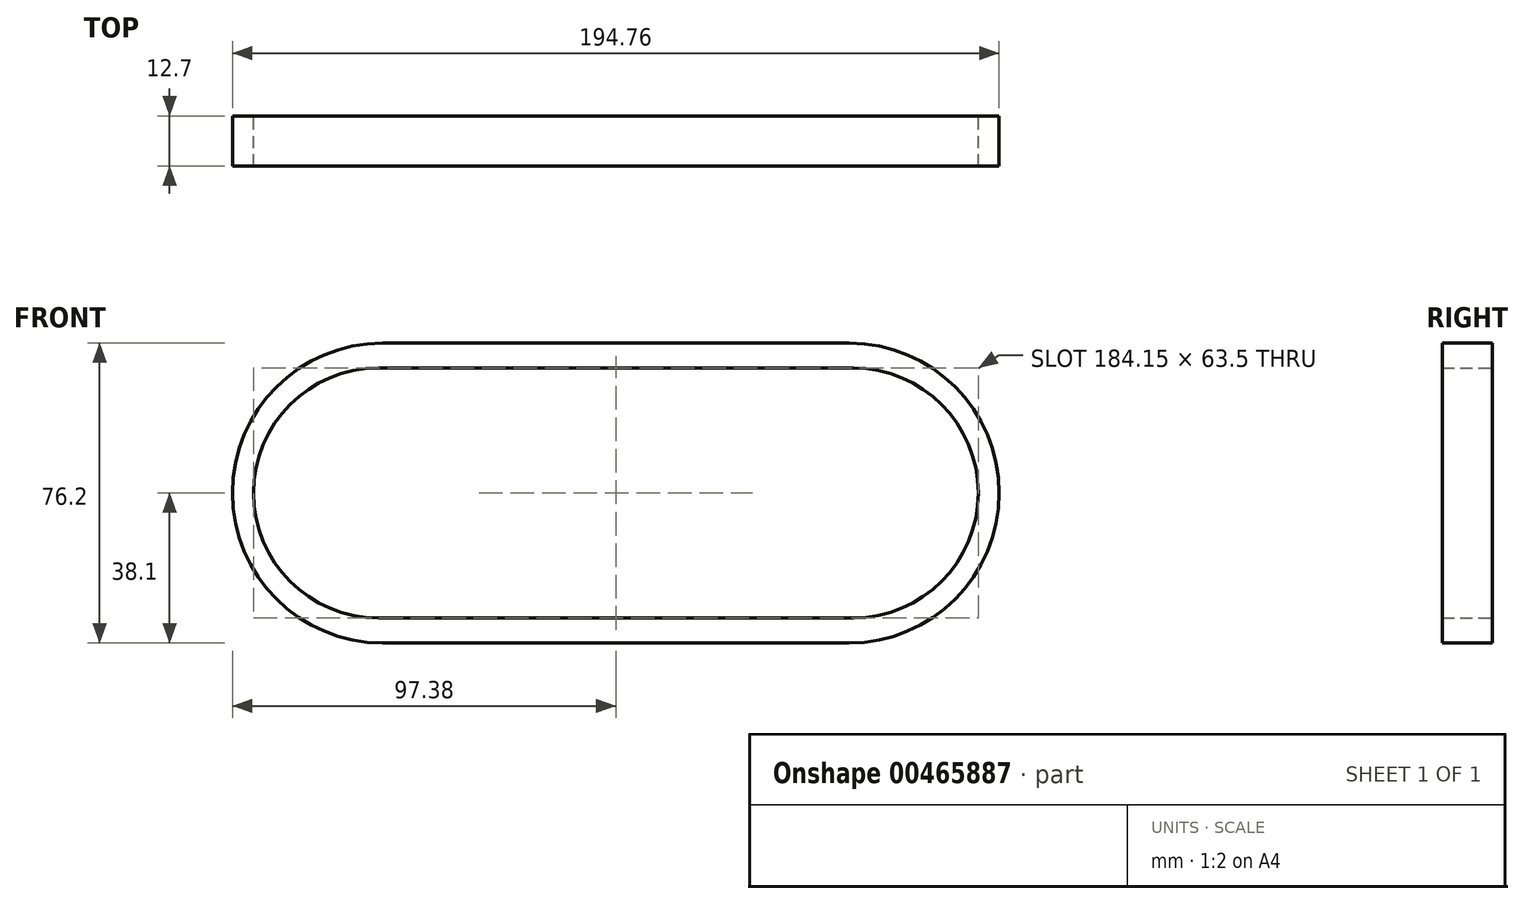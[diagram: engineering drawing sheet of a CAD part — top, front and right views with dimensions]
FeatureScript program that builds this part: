
annotation { "Feature Type Name" : "Feature", "Feature Type Description" : "" }
export const myFeature = defineFeature(function(context is Context, id is Id, definition is map)
    precondition{}
    {
        {
            var Q0;
            Q0=qCreatedBy(makeId("Front.planeOp"),FACE);
            var sketch = newSketch(context, id + "F0", { "sketchPlane" : qUnion([Q0])});
            skLineSegment(sketch, "E0.bottom", {"start": v(-59.28, 38.1) * mm, "end": v(59.28, 38.1) * mm});
            skLineSegment(sketch, "E0.top", {"start": v(-59.28, -38.1) * mm, "end": v(59.28, -38.1) * mm});
            skLineSegment(sketch, "E0.left", {"start": v(-59.28, 38.1) * mm, "end": v(-59.28, -38.1) * mm});
            skLineSegment(sketch, "E0.right", {"start": v(59.28, 38.1) * mm, "end": v(59.28, -38.1) * mm});
            skPoint(sketch, "E0.middle", {"position": v(0, 0) * mm});
            skLineSegment(sketch, "E1", {"start": v(-59.28, 38.1) * mm, "end": v(-59.28, 0) * mm});
            skCircle(sketch, "E2", {"center": v(-59.28, 0) * mm, "radius": 38.1 * mm});
            skLineSegment(sketch, "E3", {"start": v(59.28, 38.1) * mm, "end": v(59.28, 0) * mm});
            skCircle(sketch, "E4", {"center": v(59.28, 0) * mm, "radius": 38.1 * mm});
            skSolve(sketch);
        }
        {
            var Q0;
            {var subQ0=sQuery(id+"F0.wireOp",EDGE,"E0.left");Q0=makeQuery(id+"F0.imprint","IMPRINT",FACE,{"disambiguationData":[TD([[makeQuery(id+"F0.imprint","IMPRINT",EDGE,{"derivedFrom":subQ0}),-1.0]])]});}
            var Q1;
            {var subQ0=sQuery(id+"F0.wireOp",EDGE,"E0.left");Q1=makeQuery(id+"F0.imprint","IMPRINT",FACE,{"disambiguationData":[TD([[makeQuery(id+"F0.imprint","IMPRINT",EDGE,{"derivedFrom":subQ0}),1.0]])]});}
            var Q2;
            {var subQ0=sQuery(id+"F0.wireOp",EDGE,"E0.bottom");Q2=makeQuery(id+"F0.imprint","IMPRINT",FACE,{"disambiguationData":[TD([[makeQuery(id+"F0.imprint","IMPRINT",EDGE,{"derivedFrom":subQ0}),-1.0]])]});}
            var Q3;
            {var subQ0=sQuery(id+"F0.wireOp",EDGE,"E0.right");Q3=makeQuery(id+"F0.imprint","IMPRINT",FACE,{"disambiguationData":[TD([[makeQuery(id+"F0.imprint","IMPRINT",EDGE,{"derivedFrom":subQ0}),-1.0]])]});}
            var Q4;
            {var subQ0=sQuery(id+"F0.wireOp",EDGE,"E0.right");Q4=makeQuery(id+"F0.imprint","IMPRINT",FACE,{"disambiguationData":[TD([[makeQuery(id+"F0.imprint","IMPRINT",EDGE,{"derivedFrom":subQ0}),1.0]])]});}
            extrude(context, id + "F1", {"entities" : qUnion([Q0, Q1, Q2, Q3, Q4]), "depth" : 12.7 * mm, "offsetDistance" : 25.4 * mm});
        }
        {
            var Q0;
            Q0=qCreatedBy(makeId("Front.planeOp"),FACE);
            var sketch = newSketch(context, id + "F2", { "sketchPlane" : qUnion([Q0])});
            skLineSegment(sketch, "E5.bottom", {"start": v(60.33, 31.75) * mm, "end": v(-60.33, 31.75) * mm});
            skLineSegment(sketch, "E5.top", {"start": v(60.33, -31.75) * mm, "end": v(-60.33, -31.75) * mm});
            skLineSegment(sketch, "E5.left", {"start": v(60.33, 31.75) * mm, "end": v(60.33, -31.75) * mm});
            skLineSegment(sketch, "E5.right", {"start": v(-60.33, 31.75) * mm, "end": v(-60.33, -31.75) * mm});
            skPoint(sketch, "E5.middle", {"position": v(0, 0) * mm});
            skLineSegment(sketch, "E6", {"start": v(60.33, 31.75) * mm, "end": v(60.33, 0) * mm});
            skLineSegment(sketch, "E7", {"start": v(-60.33, 31.75) * mm, "end": v(-60.33, 0) * mm});
            skCircle(sketch, "E8", {"center": v(60.33, 0) * mm, "radius": 31.75 * mm});
            skCircle(sketch, "E9", {"center": v(-60.33, 0) * mm, "radius": 31.75 * mm});
            skSolve(sketch);
        }
        {
            var Q0;
            {var subQ0=sQuery(id+"F2.wireOp",EDGE,"E5.right");Q0=makeQuery(id+"F2.imprint","IMPRINT",FACE,{"disambiguationData":[TD([[makeQuery(id+"F2.imprint","IMPRINT",EDGE,{"derivedFrom":subQ0}),-1.0]])]});}
            var Q1;
            {var subQ0=sQuery(id+"F2.wireOp",EDGE,"E5.right");Q1=makeQuery(id+"F2.imprint","IMPRINT",FACE,{"disambiguationData":[TD([[makeQuery(id+"F2.imprint","IMPRINT",EDGE,{"derivedFrom":subQ0}),1.0]])]});}
            var Q2;
            {var subQ0=sQuery(id+"F2.wireOp",EDGE,"E5.bottom");Q2=makeQuery(id+"F2.imprint","IMPRINT",FACE,{"disambiguationData":[TD([[makeQuery(id+"F2.imprint","IMPRINT",EDGE,{"derivedFrom":subQ0}),1.0]])]});}
            var Q3;
            {var subQ0=sQuery(id+"F2.wireOp",EDGE,"E5.left");Q3=makeQuery(id+"F2.imprint","IMPRINT",FACE,{"disambiguationData":[TD([[makeQuery(id+"F2.imprint","IMPRINT",EDGE,{"derivedFrom":subQ0}),-1.0]])]});}
            var Q4;
            {var subQ0=sQuery(id+"F2.wireOp",EDGE,"E5.left");Q4=makeQuery(id+"F2.imprint","IMPRINT",FACE,{"disambiguationData":[TD([[makeQuery(id+"F2.imprint","IMPRINT",EDGE,{"derivedFrom":subQ0}),1.0]])]});}
            extrude(context, id + "F3", {"entities" : qUnion([Q0, Q1, Q2, Q3, Q4]), "operationType" : NewBodyOperationType.REMOVE, "oppositeDirection" : true, "depth" : -25.4 * mm, "offsetDistance" : 25.4 * mm});
        }
    });
